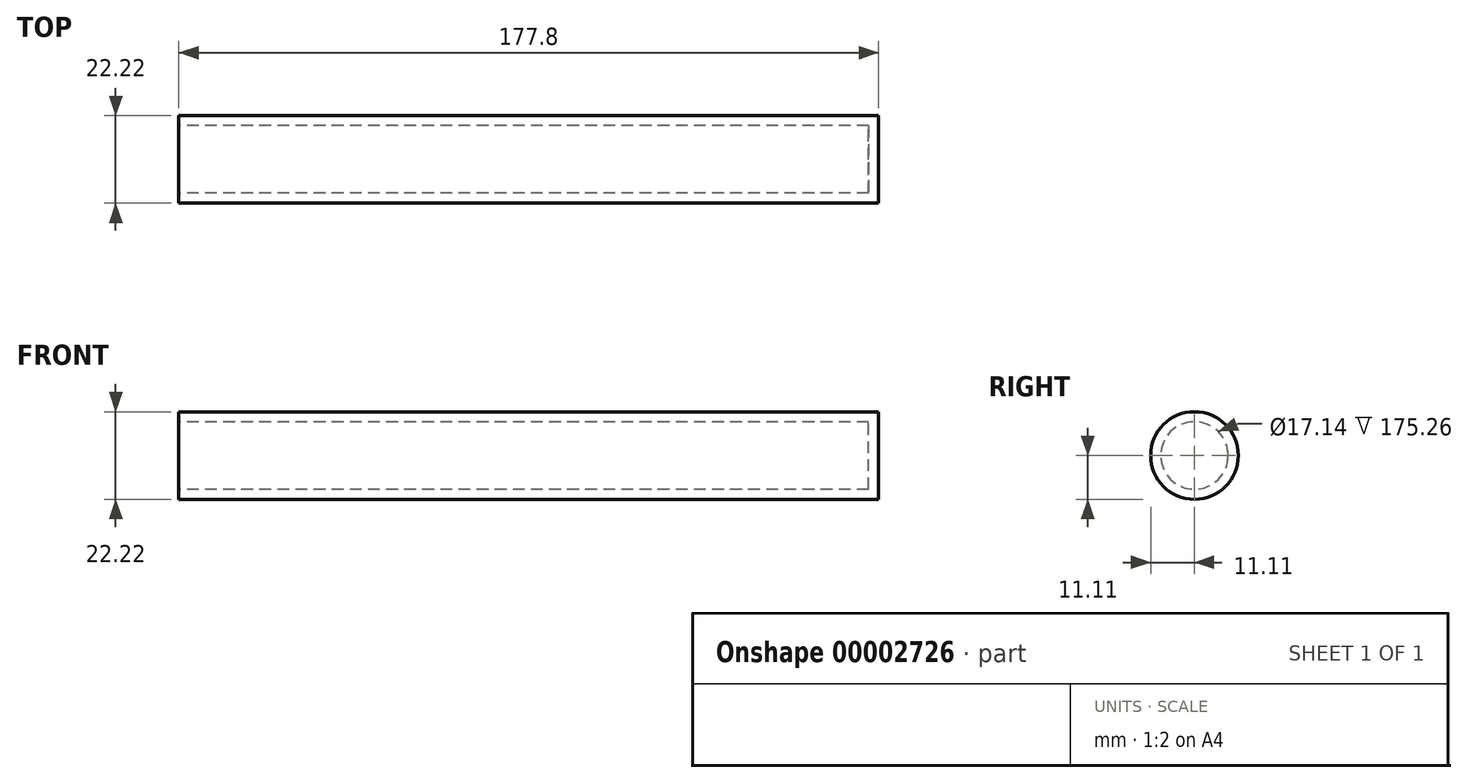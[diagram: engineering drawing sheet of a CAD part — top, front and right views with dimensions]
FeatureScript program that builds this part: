
annotation { "Feature Type Name" : "Feature", "Feature Type Description" : "" }
export const myFeature = defineFeature(function(context is Context, id is Id, definition is map)
    precondition{}
    {
        {
            var Q0;
            Q0=qCreatedBy(makeId("Right.planeOp"),FACE);
            var sketch = newSketch(context, id + "F0", { "sketchPlane" : qUnion([Q0])});
            skCircle(sketch, "E0", {"center": v(0, 0) * mm, "radius": 11.11 * mm});
            skSolve(sketch);
        }
        {
            var Q0;
            Q0=makeQuery(id+"F0.imprint","IMPRINT",FACE,{"disambiguationData":[TD([[makeQuery(id+"F0.imprint","IMPRINT",EDGE,{"derivedFrom":sQuery(id+"F0.wireOp",EDGE,"E0")}),1.0]])]});
            extrude(context, id + "F1", {"entities" : qUnion([Q0]), "depth" : 177.8 * mm});
        }
        {
            var Q0;
            Q0=makeQuery(id+"F1.opExtrude","CAP_FACE",FACE,{"disambiguationData":[OSD([sQuery(id+"F0.wireOp",EDGE,"E0")])],"isStart":true});
            shell(context, id + "F2", {"entities" : qUnion([Q0]), "thickness" : 2.54 * mm});
        }
    });
